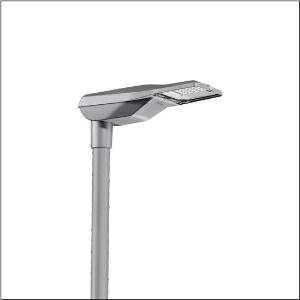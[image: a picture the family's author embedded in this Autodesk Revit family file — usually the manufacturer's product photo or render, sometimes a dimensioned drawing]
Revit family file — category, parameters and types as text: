
# Revit family: streetlight_sl_21_iq_micro___st1_5a_5xe1p31d08db_ec34
name_source: partatom
category: Lighting Fixtures
units: mm (PartAtom-declared; Revit-internal decimal feet)

## family parameters
Cut with Voids When Loaded = No
Host = Face
Light Source = No
Part Type = Normal
Room Calculation Point = No
Round Connector Dimension = Use Diameter
Shared = No

## types (1)
- --- (1 x LED, 4730 lm, 36.4 W, 3000K)
    Apparent Load = 36 VA
    CIE Flux Codes = 22 53 95 100 100
    Color Rendering = 70
    Color Temperature = 3000K
    Default Elevation = 1800 mm
    Description = Streetlight SL 21 iQ micro, mast luminaire, primary light control with lens, of PMMA, primary optical cover: cover, of toughened safety glass, transparent, light distribution: ST1.5a, light emission: direct distribution, primary light characteristic: asymmetric, installation type: post-top, side-entry, LED, High Power LED, rated luminous flux: 4.730lm, luminous efficacy: 130lm/W, light colour: 730, colour temperature: 3000K, control: Auto-Match, Temp-Guard, Lumen-Switch, Night-Set, Smart-Wire, Light-Fading, Desk-Remote (wireless, voltage-free reading and setting of iQ features in the workshop via application-optimized NFC function/RFID function), optimised constant luminous flux control (CLO 2.0), presetting dimming linear, mains connection: 220..240V, AC, 50/60Hz, start of lifetime: 36W, end of service life: 38W, reduction: 16W, luminaire housing, of diecast aluminium, powder-coated, Siteco® metallic grey (DB 702S), corrosivity category C5 mid according to DIN EN ISO 12944, please order mast flange separately, inclination adjustable: 0°, 5°, 10°, 15°, sealing non-destructively replaceable, multi-level sealing system, length: 528mm, width: 235mm, height: 110mm, mast flange for spigot size: 42mm (side-entry): 5XC10008XM4, 60/48mm (side-entry/post-top): 5XC10108XM2, 76/60mm (side-entry/post-top): 5XC10108XM1, protection rating (complete): IP66, insulation class (complete): insulation class II (safety insulation), certification: CE, ENEC, ENEC+, VDE, impact resistance: IK09, permissible operating ambient temperature for outdoor applications: -40..+50°C, standard-compliant lighting for roads and squares, packaging unit: 1 piece

Light Distribution: ST1.5a
    Height = 110 mm
    Lamp = 1 x LED
    Lamp Light Flux = 4730 lm
    Lamp Power = 36.4 W
    Lamp count = 1
    Length = 528 mm
    Luminous efficacy = 130 lm/W
    Manufacturer = Siteco
    ModVariant = No
    Model = 5XE1P31D08DB
    Number of Poles = 1
    OnlyDefault = Yes
    Power Factor = 1
    Product Name = Streetlight SL 21 iQ micro | ST1.5a
    Product group = mast luminaire | pylon top
    ProductGroupID = 6100
    Protection Class = Protection class II
    Protection Degree = IP 66
    RLX_Detail_Level = 1
    RLX_Emergency_Light_Flux = 0 lm
    RLX_Emergency_Type = 0
    RLX_Emergency_Type_DB = No
    RlxData = <blob elided: 102601 chars, md5=0cf9c037>
    Socket = socket
    Standby Power = 0 W
    System Light Flux = 4730 lm
    System Power = 36 W
    Type Comments = factory setting: luminous flux: 100 % | dim-lin: 254 | 715 mA
    Type Image = l_1006881.jpg
    URL = http://relux.com
    VarID = @adj_086205
    Voltage = 0 V
    Weight = 0.00 kg
    Width = 235 mm

## geometry (parser evidence)
native form markers: Blend x4, Sweep x10
no freeform markers — native parametric forms only
